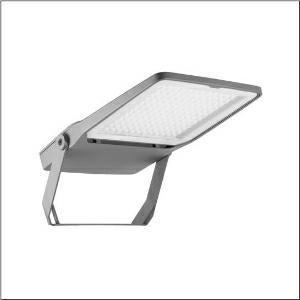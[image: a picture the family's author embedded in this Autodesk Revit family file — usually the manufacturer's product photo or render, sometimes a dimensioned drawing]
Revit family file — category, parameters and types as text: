
# Revit family: floodlight_fl_20_midi___rs17_5xa7682d3b1ac_14e5
name_source: partatom
category: Lighting Fixtures
units: mm (PartAtom-declared; Revit-internal decimal feet)

## family parameters
Cut with Voids When Loaded = No
Host = Face
Light Source = No
Part Type = Normal
Room Calculation Point = No
Round Connector Dimension = Use Diameter
Shared = No

## types (1)
- --- (1 x LED 5000K / CRI = 70 (unbekannt), 19830 lm, 5000K)
    Apparent Load = 142 VA
    CIE Flux Codes = 79 92 99 100 100
    Color Rendering = 70
    Color Temperature = 5000K
    Default Elevation = 1800 mm
    Description = Floodlight FL 20 midi, floodlight, primary light control with lens, of plastic, primary optical cover: protective disc, of toughened safety glass, transparent, light distribution: RS17, light emission: direct distribution, primary light characteristic: rotationally symmetric, installation type: surface-mounted, LED High Power LED, rated luminous flux: 19.830 lm, light colour: 750, colour temperature: 5000K, control gear: ECG Plus, control: flexible luminous flux parameterisation, time-dependent luminous flux control, digital communication interface, power reduction, overheat protection, electronic power reduction, with terminal, 5-pole, max. 2.5mm², mains connection: 220..240V, AC, 50/60Hz, rated input power: 142W, LED unit, of diecast aluminium, powder-coated, Siteco® metallic grey (DB 702S), length: 654 mm, width: 450 mm, height: 76mm, housing frame, of diecast aluminium, powder-coated, Siteco® metallic grey (DB 702S), mounting bracket, of steel, powder-coated, Siteco® metallic grey (DB 702S), DALIprotection rating (complete): IP66, insulation class (complete): insulation class II (safety insulation), certification: CE, ENEC, VDE, protection symbol: D, permissible ambient temperature for indoor applications: -40..+40°C, permissible ambient temperature for outdoor applications: -40..+50°C, standard: DIN EN 12944, packaging unit: 1 piece

Light Distribution: RS17
    Height = 76 mm
    Lamp = 1 x LED 5000K / CRI >= 70 (unbekannt)
    Lamp Light Flux = 19830 lm
    Lamp count = 1
    Length = 672 mm
    Luminous efficacy = 140 lm/W
    Manufacturer = Siteco
    ModVariant = No
    Model = 5XA7682D3B1AC
    Number of Poles = 1
    OnlyDefault = Yes
    Power Factor = 1
    Product Name = Floodlight FL 20 midi | RS17
    Product group = floodlight | pylon top
    ProductGroupID = 6101
    Protection Class = Protection class II
    Protection Degree = IP 66
    RLX_Detail_Level = 1
    RlxData = <blob elided: 92153 chars, md5=3ddf8cd8>
    Socket = socket
    Standby Power = 0 W
    System Light Flux = 19830 lm
    System Power = 142 W
    Type Comments = factory setting: luminous flux: 100 % | dim-lin: 254 | 489 mA
    Type Image = l_1005943.jpg
    URL = http://relux.com
    VarID = @adj_141957
    Voltage = 0 V
    Weight = 0.00 kg
    Width = 450 mm

## geometry (parser evidence)
native form markers: Blend x4, Sweep x14
no freeform markers — native parametric forms only
